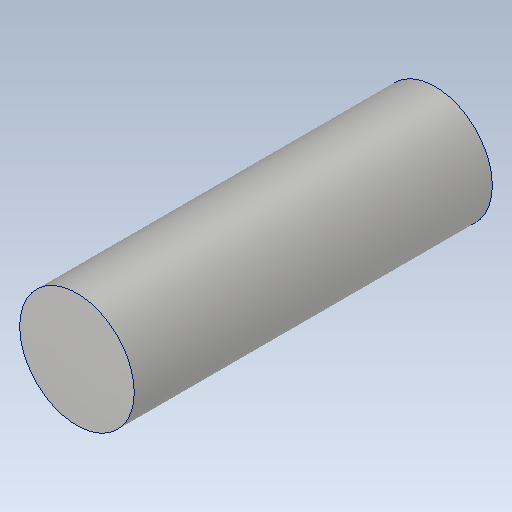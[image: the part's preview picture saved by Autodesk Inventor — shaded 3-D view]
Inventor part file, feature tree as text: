
AUTODESK INVENTOR PART (.ipt)
format: ipt  version: 2021 (Build 250183000, 183)  size: 103,936 bytes
history: native  units: in
note: dims shown in document units (in); Inventor stores cm internally (conversion verified against a paired STEP export)
features: sketch x3, extrude x2
ambient origin geometry x8: Origin, YZ Plane, XZ Plane, XY Plane, X Axis, Y Axis, Z Axis, Center Point
bodies: Solid1 (feature_tree)
feature tree (5):
  sketch  "Sketch1"  dims[d0=1.5748in d1=1.9685in d2=0.0in]
  extrude  "Extrusion1"  Depth=1.9685in TaperAngle=0.0deg
  extrude  "Extrusion2"  Depth=2.9528in TaperAngle=0.0deg
  sketch  "Sketch2"  dims[d3=1.5748in d4=2.9528in d5=0.0in]
  sketch  "Sketch3"
